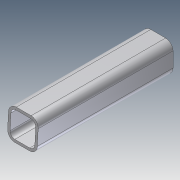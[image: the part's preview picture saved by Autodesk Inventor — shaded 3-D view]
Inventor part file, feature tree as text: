
AUTODESK INVENTOR PART (.ipt)
format: ipt  version: unknown  size: 194,048 bytes
history: native  units: in
note: dims shown in document units (in); Inventor stores cm internally (conversion verified against a paired STEP export)
features: extrude x2, sketch x2
ambient origin geometry x8: Origin, YZ Plane, XZ Plane, XY Plane, X Axis, Y Axis, Z Axis, Center Point
bodies: Solid1 (feature_tree)
feature tree (4):
  extrude  "Extrusion1"  Depth=0.375in
  extrude  "Extrusion2"  Depth=6.875in TaperAngle=0.0deg
  sketch  "Sketch1"  dims[d0=1.5in d1=0.375in]
  sketch  "Sketch2"  dims[d2=0.125in d3=6.875in d4=0.0in d5=0.0206in d6=7.0in d7=0.0in]
